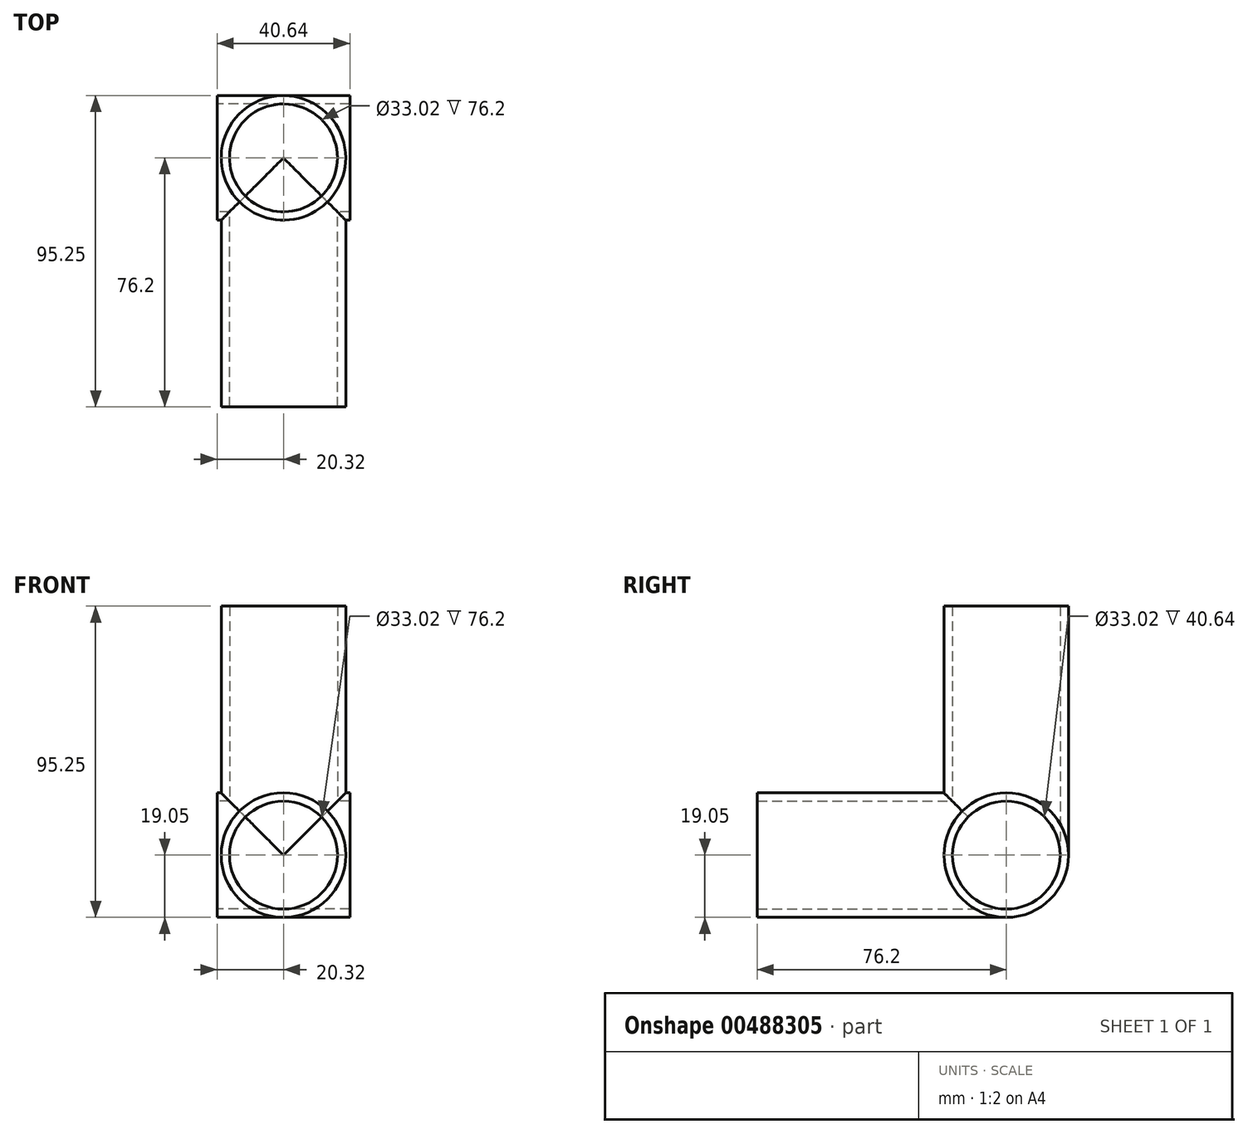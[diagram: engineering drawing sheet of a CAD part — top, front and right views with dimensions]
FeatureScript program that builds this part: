
annotation { "Feature Type Name" : "Feature", "Feature Type Description" : "" }
export const myFeature = defineFeature(function(context is Context, id is Id, definition is map)
    precondition{}
    {
        {
            var Q0;
            Q0=qCreatedBy(makeId("Front.planeOp"),FACE);
            var sketch = newSketch(context, id + "F0", { "sketchPlane" : qUnion([Q0])});
            skCircle(sketch, "E0", {"center": v(0, 0) * mm, "radius": 19.05 * mm});
            skSolve(sketch);
        }
        {
            var Q0;
            Q0=makeQuery(id+"F0.imprint","IMPRINT",FACE,{"disambiguationData":[TD([[makeQuery(id+"F0.imprint","IMPRINT",EDGE,{"derivedFrom":sQuery(id+"F0.wireOp",EDGE,"E0")}),1.0]])]});
            extrude(context, id + "F1", {"entities" : qUnion([Q0]), "depth" : 76.2 * mm});
        }
        {
            var Q0;
            Q0=qCreatedBy(makeId("Right.planeOp"),FACE);
            var sketch = newSketch(context, id + "F2", { "sketchPlane" : qUnion([Q0])});
            skCircle(sketch, "E1", {"center": v(0, 0) * mm, "radius": 19.05 * mm});
            skSolve(sketch);
        }
        {
            var Q0;
            Q0=makeQuery(id+"F2.imprint","IMPRINT",FACE,{"disambiguationData":[TD([[makeQuery(id+"F2.imprint","IMPRINT",EDGE,{"derivedFrom":sQuery(id+"F2.wireOp",EDGE,"E1")}),1.0]])]});
            extrude(context, id + "F3", {"entities" : qUnion([Q0]), "endBound" : BoundingType.SYMMETRIC, "depth" : 40.64 * mm});
        }
        {
            var Q0;
            Q0=qCreatedBy(makeId("Top.planeOp"),FACE);
            var sketch = newSketch(context, id + "F4", { "sketchPlane" : qUnion([Q0])});
            skCircle(sketch, "E2", {"center": v(0, 0) * mm, "radius": 19.05 * mm});
            skSolve(sketch);
        }
        {
            var Q0;
            Q0=qSketchRegion(id+"F4",true);
            extrude(context, id + "F5", {"entities" : qUnion([Q0]), "operationType" : NewBodyOperationType.ADD, "depth" : 76.2 * mm});
        }
        {
            var Q0;
            Q0=sQuery(id+"F4.wireOp",VERTEX,"E2.center");
            var Q1;
            Q1=makeQuery(id+"F1.opExtrude","SWEPT_BODY",BODY,{"disambiguationData":[OSD([sQuery(id+"F0.wireOp",EDGE,"E0")])]});
            hole(context, id + "F6", {"style" : HoleStyle.SIMPLE, "endStyle" : HoleEndStyle.THROUGH, "oppositeDirection" : true, "holeDiameter" : 33.02 * mm, "isTappedThrough" : true, "tappedDepth" : 12.7 * mm, "tapClearance" : 3, "startFromSketch" : true, "locations" : qUnion([Q0]), "scope" : qUnion([Q1])});
        }
        {
            var Q0;
            Q0=sQuery(id+"F2.wireOp",VERTEX,"E1.center");
            var Q1;
            Q1=makeQuery(id+"F1.opExtrude","SWEPT_BODY",BODY,{"disambiguationData":[OSD([sQuery(id+"F0.wireOp",EDGE,"E0")])]});
            var Q2;
            Q2=makeQuery(id+"F3.opExtrude","SWEPT_BODY",BODY,{"disambiguationData":[OSD([sQuery(id+"F2.wireOp",EDGE,"E1")])]});
            hole(context, id + "F7", {"style" : HoleStyle.SIMPLE, "endStyle" : HoleEndStyle.THROUGH, "oppositeDirection" : true, "holeDiameter" : 33.02 * mm, "isTappedThrough" : true, "tappedDepth" : 12.7 * mm, "tapClearance" : 3, "startFromSketch" : true, "locations" : qUnion([Q0]), "scope" : qUnion([Q1, Q2])});
        }
        {
            var Q0;
            Q0=sQuery(id+"F2.wireOp",VERTEX,"E1.center");
            var Q1;
            Q1=makeQuery(id+"F3.opExtrude","SWEPT_BODY",BODY,{"disambiguationData":[OSD([sQuery(id+"F2.wireOp",EDGE,"E1")])]});
            var Q2;
            Q2=makeQuery(id+"F1.opExtrude","SWEPT_BODY",BODY,{"disambiguationData":[OSD([sQuery(id+"F0.wireOp",EDGE,"E0")])]});
            hole(context, id + "F8", {"style" : HoleStyle.SIMPLE, "endStyle" : HoleEndStyle.THROUGH, "holeDiameter" : 33.02 * mm, "isTappedThrough" : true, "tappedDepth" : 12.7 * mm, "tapClearance" : 3, "startFromSketch" : true, "locations" : qUnion([Q0]), "scope" : qUnion([Q1, Q2])});
        }
        {
            var Q0;
            Q0=sQuery(id+"F0.wireOp",VERTEX,"E0.center");
            var Q1;
            Q1=sQuery(id+"F4.wireOp",VERTEX,"E2.center");
            var Q2;
            Q2=makeQuery(id+"F3.opExtrude","SWEPT_BODY",BODY,{"disambiguationData":[OSD([sQuery(id+"F2.wireOp",EDGE,"E1")])]});
            var Q3;
            Q3=makeQuery(id+"F1.opExtrude","SWEPT_BODY",BODY,{"disambiguationData":[OSD([sQuery(id+"F0.wireOp",EDGE,"E0")])]});
            hole(context, id + "F9", {"style" : HoleStyle.SIMPLE, "endStyle" : HoleEndStyle.BLIND, "oppositeDirection" : true, "holeDiameter" : 33.02 * mm, "holeDepth" : 63.5 * mm, "isTappedThrough" : true, "tappedDepth" : 12.7 * mm, "tapClearance" : 3, "locations" : qUnion([Q0, Q1]), "scope" : qUnion([Q2, Q3])});
        }
    });
